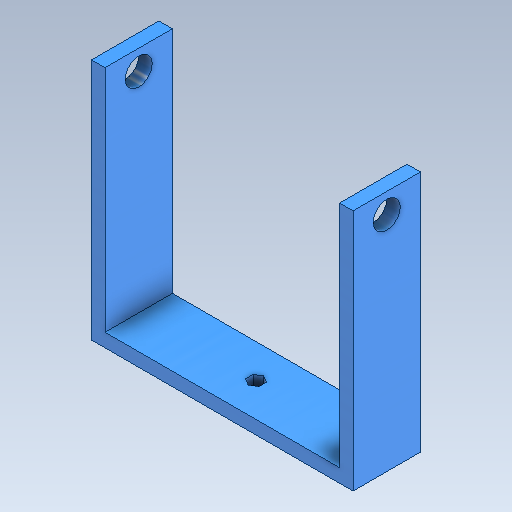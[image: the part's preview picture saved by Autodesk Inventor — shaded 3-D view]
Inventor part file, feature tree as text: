
AUTODESK INVENTOR PART (.ipt)
format: ipt  version: 2021.2 (Build 252289000, 289)  size: 146,944 bytes
history: native  units: in
note: dims shown in document units (in); Inventor stores cm internally (conversion verified against a paired STEP export)
features: extrude x4, sketch x4
ambient origin geometry x8: Origin, YZ Plane, XZ Plane, XY Plane, X Axis, Y Axis, Z Axis, Center Point
bodies: Solid1 (feature_tree)
feature tree (8):
  extrude  "Extrusion1"  Depth=2.5in
  extrude  "Extrusion2"  Depth=0.5in
  extrude  "Extrusion3"  Depth=8.5in TaperAngle=0.0deg
  extrude  "Extrusion4"  Depth=0.5in
  sketch  "Sketch1"  dims[d0=9.7in d1=2.5in]
  sketch  "Sketch2"  dims[d2=0.5in d3=0.0in d4=0.5in]
  sketch  "Sketch3"  dims[d5=0.5in d6=8.5in d7=0.0in]
  sketch  "Sketch4"  dims[d8=1.0in d9=0.25in d10=0.0in d11=0.0in d13=0.5in d14=0.0in d15=0.0in]
